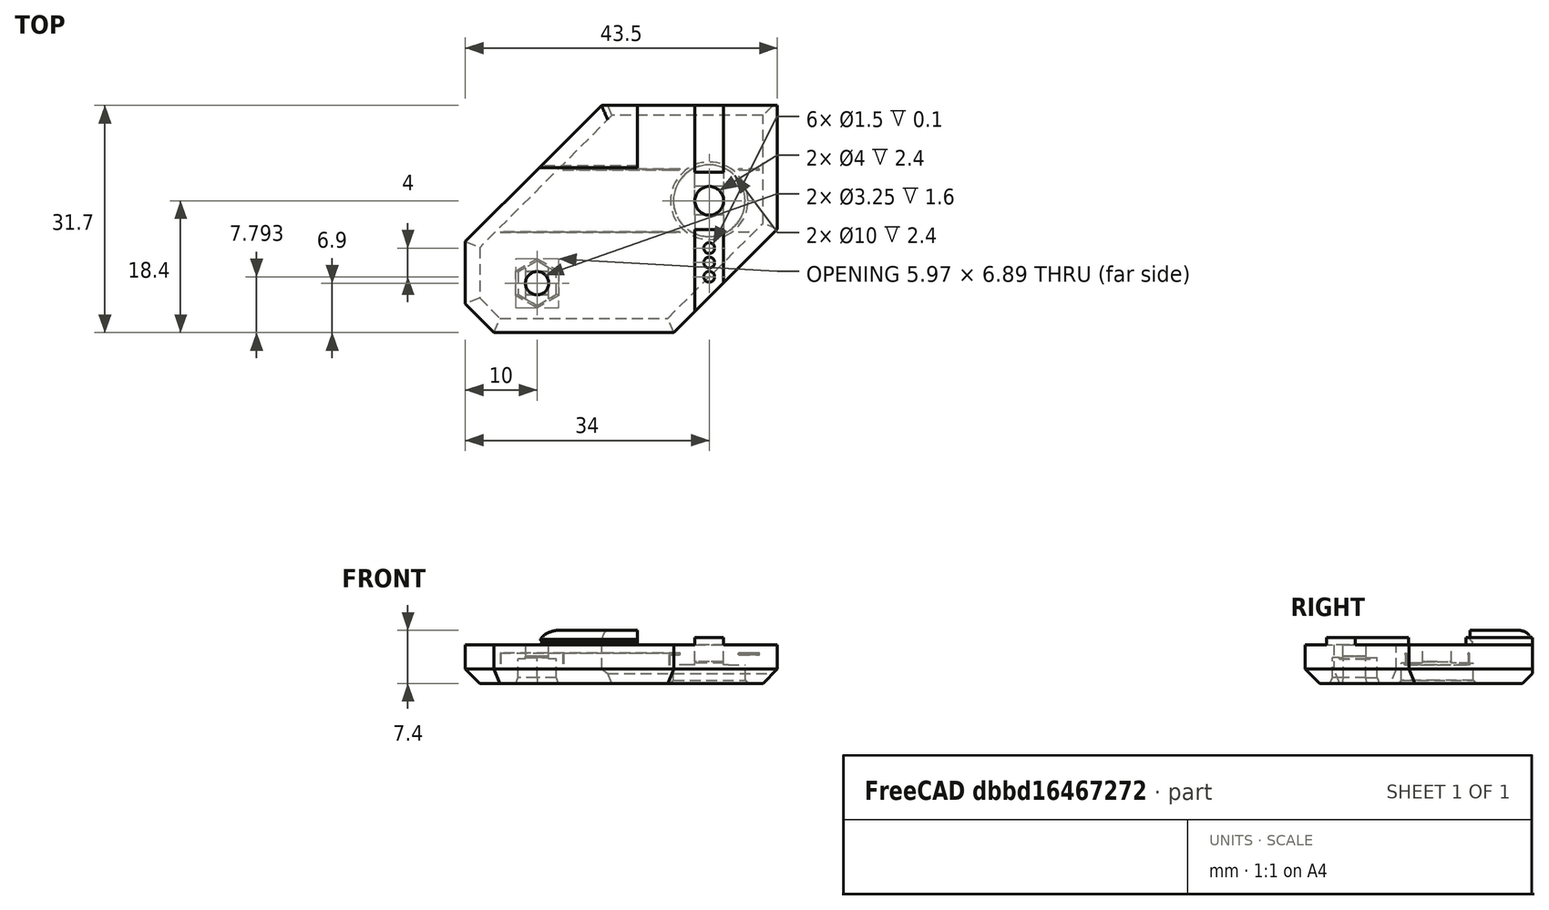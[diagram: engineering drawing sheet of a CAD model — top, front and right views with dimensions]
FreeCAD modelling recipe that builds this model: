
FCSTD DOCUMENT  (FreeCAD 0.18R14555 (Git shallow))
Label: base-bottom
License: All rights reserved
LicenseURL: http://en.wikipedia.org/wiki/All_rights_reserved
objects: Part::Feature×4, Part::Cut×3, Part::Box×2, App::Part×1, Part::MultiFuse×1
note: 10 computed .brp shape members not serialized (recipe doc carries the construction recipe); baked Part::Feature solids carry a one-line shape summary decoded from their .brp

FEATURE [Part::Feature] Part__Feature  label="rambo_base_lower_mount"
  Placement = pos=(0,0,0) rot=(1,0,0;3.14159rad)
  shape: bbox 43.52 x 31.72 x 7.416 mm, 91 faces (baked)
FEATURE [Part::Feature] Cut001001  label="m5-to-m4-bolt-hole-big001"
  Placement = pos=(24,12,2.6) rot=(0,0,1;1.5708rad)
  shape: bbox 12 x 12 x 3 mm, 15 faces (baked)
FEATURE [Part::Box] Box004  label="Cube004"
  AttacherType = Attacher::AttachEngine3D
  Height = 10
  Length = 15
  Placement = pos=(16.4,0,5.4) rot=(0,0,1;0rad)
  Width = 20
FEATURE [Part::Cut] Cut001002
  Base = -> Cut001001
  Placement = pos=(0,-0.5,0) rot=(0,0,1;0rad)
  Tool = -> Box004
FEATURE [Part::Box] Box  label="Cube"
  AttacherType = Attacher::AttachEngine3D
  Height = 2
  Length = 8
  Placement = pos=(20,7.5,5.4) rot=(0,0,1;0rad)
  Width = 8
FEATURE [App::Part] rambo_base_lower_mount_v1001  label="rambo_base_lower_mount v002"
  Origin = -> Origin004
FEATURE [Part::Feature] Part__Feature001  label="t-slot-align"
  Placement = pos=(18.77,-16.2,5.4) rot=(0.57735,0.57735,0.57735;2.0944rad)
  shape: bbox 10.45 x 60 x 5 mm, 10 faces (baked)
FEATURE [Part::Cut] Cut
  Base = -> Part__Feature
  Tool = -> Part__Feature001
FEATURE [Part::Cut] Cut001003
  Base = -> Cut
  Tool = -> Box
FEATURE [Part::MultiFuse] Fusion
  Shapes = -> [Cut001003,Cut001002]
FEATURE [Part::Feature] Fusion001
  shape: bbox 43.52 x 31.72 x 7.416 mm, 105 faces (baked)
